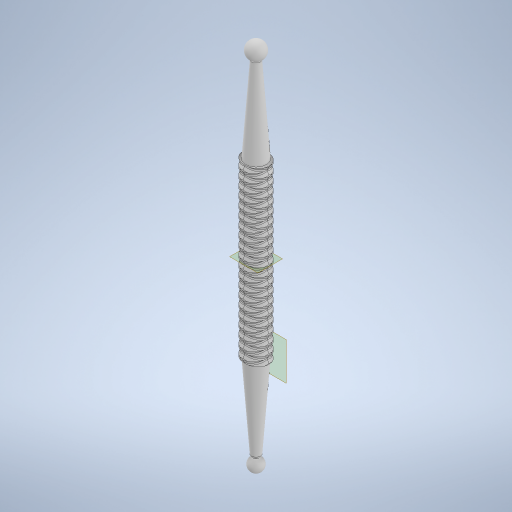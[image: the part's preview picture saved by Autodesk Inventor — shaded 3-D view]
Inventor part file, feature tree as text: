
AUTODESK INVENTOR PART (.ipt)
format: ipt  version: 2024 (Build 280153000, 153)  size: 2,787,840 bytes
history: native  units: mm
features: sketch x13, chamfer x10, extrude x5, helix x4, revolve x3, plane x2, fillet x1
ambient origin geometry x8: Origin, YZ Plane, XZ Plane, XY Plane, X Axis, Y Axis, Z Axis, Center Point
bodies: Solid1 (feature_tree)
feature tree (38):
  extrude  "Extrusion1"  Depth=100.0mm TaperAngle=0.0deg
  helix  "Coil1"  [1 undecoded]
  helix  "Coil2"  [1 undecoded]
  helix  "Coil3"  [1 undecoded]
  helix  "Coil4"  [1 undecoded]
  chamfer  "Chamfer1"  Distance=1.0mm Angle=45.0deg
  chamfer  "Chamfer2"  Distance=1.0mm Angle=45.0deg
  chamfer  "Chamfer3"  Distance=1.0mm Angle=45.0deg
  chamfer  "Chamfer4"  Distance=1.0mm Angle=45.0deg
  chamfer  "Chamfer5"  Distance=1.0mm Angle=45.0deg
  chamfer  "Chamfer6"  Distance=1.0mm Angle=45.0deg
  chamfer  "Chamfer7"  Distance=1.0mm Angle=45.0deg
  chamfer  "Chamfer8"  Distance=50.0mm
  extrude  "Extrusion2"  [1 undecoded]
  chamfer  "Chamfer9"  Distance=50.0mm
  plane  "Work Plane4"
  extrude  "Extrusion3"  Depth=5.0mm
  chamfer  "Chamfer10"  Distance=3.0mm
  sketch  "Sketch15"  dims[d71=12.0mm d72=50.0mm d73=0.0mm]
  revolve  "Revolution4"  [1 undecoded]
  fillet  "Fillet1"  Radius=1.0mm
  sketch  "Sketch18"  dims[d82=90.0deg]
  sketch  "Sketch22"  dims[d83=2.0mm]
  plane  "Work Plane6"
  sketch  "Sketch23"  dims[d97=8.0mm]
  extrude  "Extrusion4"  Depth=1.0mm TaperAngle=0.0deg
  extrude  "Extrusion5"  Depth=8.0mm
  revolve  "Revolution6"  Angle=90.0deg
  revolve  "Revolution7"  [1 undecoded]
  sketch  "Sketch1"  dims[d0=15.0mm d1=100.0mm d2=0.0mm d3=2.0mm]
  sketch  "Sketch2"  dims[d4=10.0mm d5=10.0mm d6=100.0mm d7=0.0mm d8=90.0deg d9=90.0deg d10=0.0mm d11=0.0mm]
  sketch  "Sketch4"  dims[d12=10.0mm d13=10.0mm d14=100.0mm d15=0.0mm d16=90.0deg d17=90.0deg d18=0.0mm d19=0.0mm d20=2.0mm]
  sketch  "Sketch5"  dims[d21=10.0mm d22=10.0mm d23=100.0mm d24=0.0mm d25=90.0deg d26=90.0deg d27=0.0mm d28=0.0mm d29=2.0mm]
  sketch  "Sketch6"  dims[d30=10.0mm d31=10.0mm d32=100.0mm d33=0.0mm d34=90.0deg d35=90.0deg d36=0.0mm d37=0.0mm d38=1.0mm d39=2.0mm d40=45.0deg d41=1.0mm d42=2.0mm d43=45.0deg d44=1.0mm d45=2.0mm d46=45.0deg d47=1.0mm d48=2.0mm d49=45.0deg d50=1.0mm d51=2.0mm d52=45.0deg d53=1.0mm d54=2.0mm d55=45.0deg d56=1.0mm d57=2.0mm d58=45.0deg d59=1.0mm d60=2.0mm d61=45.0deg]
  sketch  "Sketch8"  dims[d62=12.0mm d63=50.0mm d64=0.0mm]
  sketch  "Sketch11"  dims[d65=50.0mm d66=50.0mm d67=0.698132mm d69=-50.0mm]
  sketch  "Sketch16"  dims[d74=50.0mm d75=50.0mm d76=0.698132mm d81=5.0mm]
  sketch  "Sketch24"  dims[d98=1.0mm d102=3.0mm d103=0.0mm d106=8.0mm d107=1.0mm d108=3.0mm d109=0.0mm d110=8.0mm d111=90.0deg d113=2.0mm d114=1.0mm d116=10.0mm d117=90.0deg d118=1.0mm]
note: 7 required parameter values undecoded (feature->parameter linkage not recoverable at this tier; creation-order binding heuristic only, values carry confidence <= 0.55)